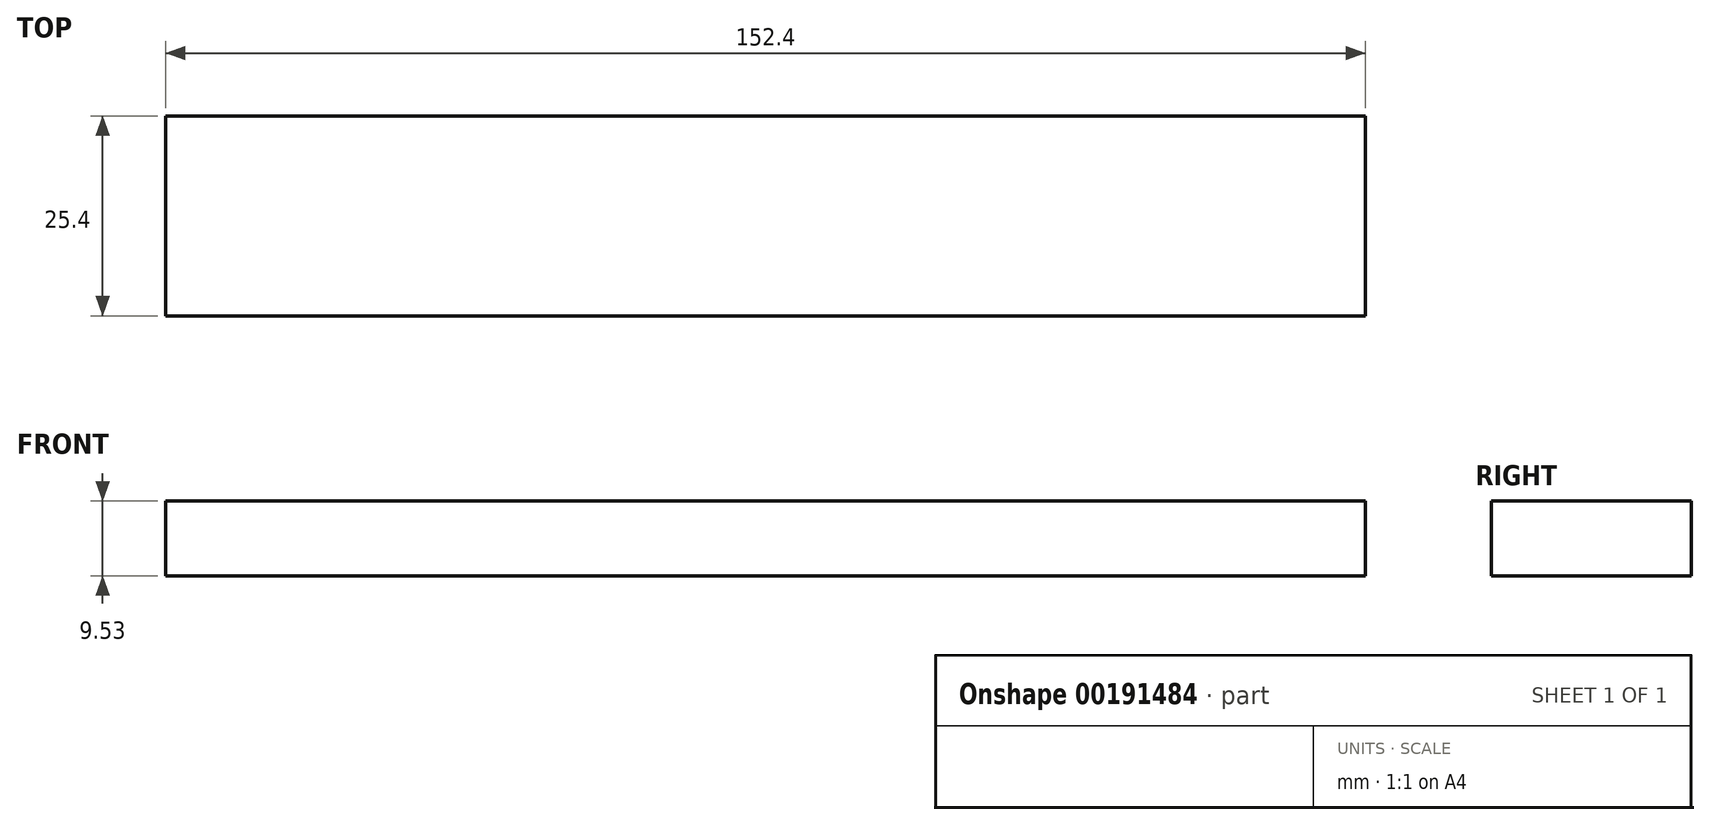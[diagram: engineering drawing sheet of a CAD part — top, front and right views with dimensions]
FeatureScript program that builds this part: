
annotation { "Feature Type Name" : "Feature", "Feature Type Description" : "" }
export const myFeature = defineFeature(function(context is Context, id is Id, definition is map)
    precondition{}
    {
        {
            var Q0;
            Q0=qCreatedBy(makeId("Top.planeOp"),FACE);
            var sketch = newSketch(context, id + "F0", { "sketchPlane" : qUnion([Q0])});
            skLineSegment(sketch, "E0.bottom", {"start": v(0, 0) * mm, "end": v(152.4, 0) * mm});
            skLineSegment(sketch, "E0.top", {"start": v(0, 25.4) * mm, "end": v(152.4, 25.4) * mm});
            skLineSegment(sketch, "E0.left", {"start": v(0, 0) * mm, "end": v(0, 25.4) * mm});
            skLineSegment(sketch, "E0.right", {"start": v(152.4, 0) * mm, "end": v(152.4, 25.4) * mm});
            skSolve(sketch);
        }
        {
            var Q0;
            Q0 = qSketchRegion(id + "F0", true);
            extrude(context, id + "F1", {"entities" : qUnion([Q0]), "depth" : 9.52 * mm});
        }
        {
            var Q0;
            Q0=qCreatedBy(makeId("Top.planeOp"),FACE);
            var sketch = newSketch(context, id + "F2", { "sketchPlane" : qUnion([Q0])});
            skLineSegment(sketch, "E1", {"start": v(0, 12.7) * mm, "end": v(163.65, 12.7) * mm});
            skCircle(sketch, "E2", {"center": v(11.55, 12.7) * mm, "radius": 3.45 * mm});
            skCircle(sketch, "E3", {"center": v(29.83, 12.7) * mm, "radius": 3.45 * mm});
            skCircle(sketch, "E4", {"center": v(45.48, 12.7) * mm, "radius": 3.45 * mm});
            skCircle(sketch, "E5", {"center": v(62.25, 12.7) * mm, "radius": 3.45 * mm});
            skCircle(sketch, "E6", {"center": v(78.13, 12.7) * mm, "radius": 3.45 * mm});
            skSolve(sketch);
        }
        {
            var Q0;
            Q0=sQuery(id+"F2.wireOp",EDGE,"E2");
            var Q1;
            Q1=sQuery(id+"F2.wireOp",EDGE,"E3");
            var Q2;
            Q2=sQuery(id+"F2.wireOp",EDGE,"E4");
            var Q3;
            Q3=sQuery(id+"F2.wireOp",EDGE,"E5");
            var Q4;
            Q4=sQuery(id+"F2.wireOp",EDGE,"E6");
            extrude(context, id + "F3", {"bodyType" : ToolBodyType.SURFACE, "surfaceEntities" : qUnion([Q0, Q1, Q2, Q3, Q4]), "endBound" : BoundingType.UP_TO_NEXT, "depth" : 25.4 * mm});
        }
    });
